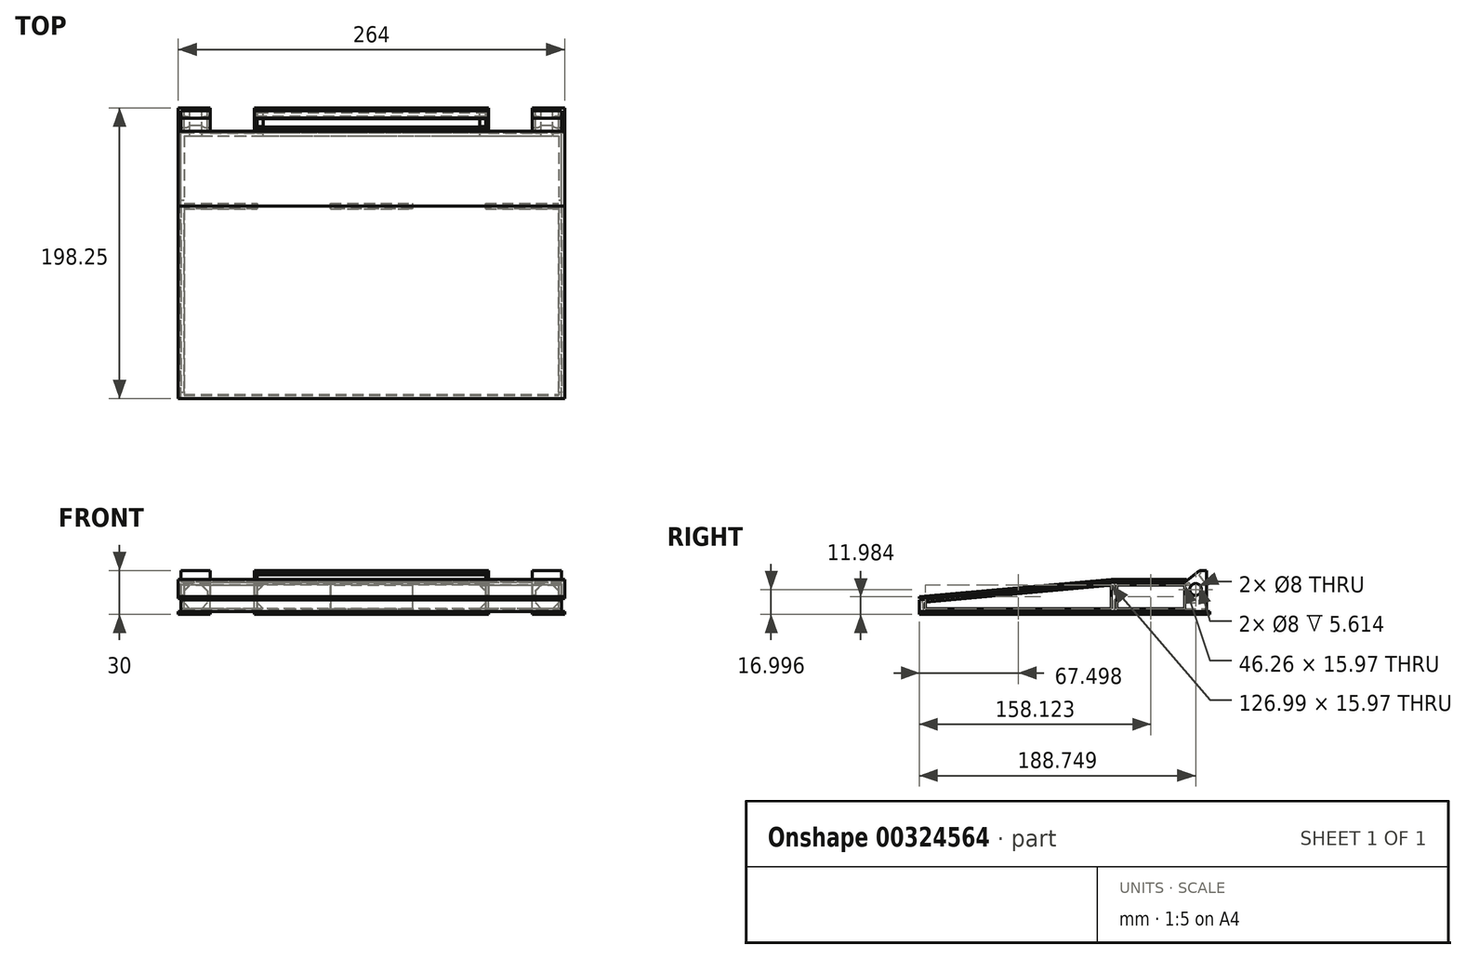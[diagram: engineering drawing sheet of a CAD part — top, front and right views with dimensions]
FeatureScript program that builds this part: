
annotation { "Feature Type Name" : "Feature", "Feature Type Description" : "" }
export const myFeature = defineFeature(function(context is Context, id is Id, definition is map)
    precondition{}
    {
        {
            var Q0;
            Q0=qCreatedBy(makeId("Right.planeOp"),FACE);
            var sketch = newSketch(context, id + "F0", { "sketchPlane" : qUnion([Q0])});
            skLineSegment(sketch, "E0", {"start": v(-99.2, 0) * mm, "end": v(-99.2, 8) * mm});
            skLineSegment(sketch, "E1", {"start": v(-99.2, 8) * mm, "end": v(32.05, 20) * mm});
            skLineSegment(sketch, "E2", {"start": v(32.05, 20) * mm, "end": v(97.05, 20) * mm});
            skLineSegment(sketch, "E3", {"start": v(97.05, 0) * mm, "end": v(97.05, 20) * mm});
            skLineSegment(sketch, "E4", {"start": v(-99.2, 0) * mm, "end": v(97.05, 0) * mm});
            skLineSegment(sketch, "E5", {"start": v(97.05, 20) * mm, "end": v(97.05, 28) * mm});
            skLineSegment(sketch, "E6", {"start": v(97.05, 28) * mm, "end": v(92.05, 28) * mm});
            skLineSegment(sketch, "E7", {"start": v(92.05, 28) * mm, "end": v(82.05, 20) * mm});
            skLineSegment(sketch, "E8", {"start": v(-95.2, 6.36) * mm, "end": v(-95.2, 2) * mm});
            skLineSegment(sketch, "E9", {"start": v(-95.2, 2) * mm, "end": v(31.8, 2) * mm});
            skLineSegment(sketch, "E10", {"start": v(31.8, 2) * mm, "end": v(31.8, 17.97) * mm});
            skLineSegment(sketch, "E11", {"start": v(31.8, 17.97) * mm, "end": v(-95.2, 6.36) * mm});
            skLineSegment(sketch, "E12.bottom", {"start": v(35.8, 17.97) * mm, "end": v(82.05, 17.97) * mm});
            skLineSegment(sketch, "E12.top", {"start": v(35.8, 2) * mm, "end": v(82.05, 2) * mm});
            skLineSegment(sketch, "E12.left", {"start": v(35.8, 17.97) * mm, "end": v(35.8, 2) * mm});
            skLineSegment(sketch, "E12.right", {"start": v(82.05, 17.97) * mm, "end": v(82.05, 2) * mm});
            skLineSegment(sketch, "E13", {"start": v(97.05, 10) * mm, "end": v(82.05, 9.98) * mm});
            skLineSegment(sketch, "E14", {"start": v(-99.2, 9) * mm, "end": v(32.05, 21) * mm});
            skLineSegment(sketch, "E15", {"start": v(32.05, 21) * mm, "end": v(82.05, 21) * mm});
            skLineSegment(sketch, "E16", {"start": v(82.05, 21) * mm, "end": v(83.3, 22) * mm});
            skLineSegment(sketch, "E17", {"start": v(83.3, 22) * mm, "end": v(32, 22) * mm});
            skLineSegment(sketch, "E18", {"start": v(32, 22) * mm, "end": v(-99.2, 10) * mm});
            skLineSegment(sketch, "E19", {"start": v(-99.2, 10) * mm, "end": v(-99.2, 9) * mm});
            skLineSegment(sketch, "E20", {"start": v(32, 23) * mm, "end": v(-98.9, 11.03) * mm});
            skLineSegment(sketch, "E21", {"start": v(-98.9, 11.03) * mm, "end": v(-98.9, 22) * mm});
            skLineSegment(sketch, "E22", {"start": v(88.6, 28) * mm, "end": v(82.35, 23) * mm});
            skLineSegment(sketch, "E23", {"start": v(82.35, 23) * mm, "end": v(32, 23) * mm});
            skLineSegment(sketch, "E24", {"start": v(88.6, 28) * mm, "end": v(-98.9, 28) * mm});
            skLineSegment(sketch, "E25", {"start": v(-98.9, 28) * mm, "end": v(-98.9, 22) * mm});
            skCircle(sketch, "E26", {"center": v(89.55, 15) * mm, "radius": 4 * mm});
            skSolve(sketch);
        }
        {
            var Q0;
            {var subQ0=sQuery(id+"F0.wireOp",EDGE,"E5");Q0=makeQuery(id+"F0.imprint","IMPRINT",FACE,{"disambiguationData":[TD([[makeQuery(id+"F0.imprint","IMPRINT",EDGE,{"derivedFrom":subQ0}),1.0]])]});}
            var Q1;
            Q1=makeQuery(id+"F0.imprint","IMPRINT",FACE,{"disambiguationData":[TD([[makeQuery(id+"F0.imprint","IMPRINT",EDGE,{"derivedFrom":sQuery(id+"F0.wireOp",EDGE,"E0")}),-1.0]])]});
            extrude(context, id + "F1", {"entities" : qUnion([Q0, Q1]), "depth" : 130 * mm, "hasSecondDirection" : true, "secondDirectionOppositeDirection" : true, "secondDirectionDepth" : 130 * mm});
        }
        {
            var Q0;
            Q0=makeQuery(id+"F1.opExtrude","SWEPT_FACE",FACE,{"disambiguationData":[OSD([sQuery(id+"F0.wireOp",EDGE,"E1")])]});
            var sketch = newSketch(context, id + "F2", { "sketchPlane" : qUnion([Q0])});
            skLineSegment(sketch, "E27.top", {"start": v(-130, -98.06) * mm, "end": v(130, -98.06) * mm});
            skLineSegment(sketch, "E28", {"start": v(-130, -98.06) * mm, "end": v(-130, 33.74) * mm});
            skLineSegment(sketch, "E29", {"start": v(-130, 33.74) * mm, "end": v(130, 33.74) * mm});
            skLineSegment(sketch, "E30", {"start": v(130, 33.74) * mm, "end": v(130, -98.06) * mm});
            skLineSegment(sketch, "E31.bottom", {"start": v(-128, 31.74) * mm, "end": v(128, 31.74) * mm});
            skLineSegment(sketch, "E31.top", {"start": v(-128, -96.06) * mm, "end": v(128, -96.06) * mm});
            skLineSegment(sketch, "E31.left", {"start": v(-128, 31.74) * mm, "end": v(-128, -96.06) * mm});
            skLineSegment(sketch, "E31.right", {"start": v(128, 31.74) * mm, "end": v(128, -96.06) * mm});
            skLineSegment(sketch, "E32", {"start": v(-128, 31.74) * mm, "end": v(-128, 33.74) * mm});
            skLineSegment(sketch, "E33", {"start": v(128, 31.74) * mm, "end": v(128, 33.74) * mm});
            skLineSegment(sketch, "E34", {"start": v(-28, 33.74) * mm, "end": v(-28, 31.74) * mm});
            skLineSegment(sketch, "E35", {"start": v(28, 33.74) * mm, "end": v(28, 31.74) * mm});
            skLineSegment(sketch, "E36", {"start": v(78, 33.74) * mm, "end": v(78, 31.74) * mm});
            skLineSegment(sketch, "E37", {"start": v(-78, 33.74) * mm, "end": v(-78, 31.74) * mm});
            skSolve(sketch);
        }
        {
            var Q0;
            Q0=makeQuery(id+"F1.opExtrude","SWEPT_FACE",FACE,{"disambiguationData":[OSD([sQuery(id+"F0.wireOp",EDGE,"E2")])]});
            var sketch = newSketch(context, id + "F3", { "sketchPlane" : qUnion([Q0])});
            skLineSegment(sketch, "E38.bottom", {"start": v(-130, 32.05) * mm, "end": v(130, 32.05) * mm});
            skLineSegment(sketch, "E38.top", {"start": v(-130, 82.05) * mm, "end": v(130, 82.05) * mm});
            skLineSegment(sketch, "E38.left", {"start": v(-130, 32.05) * mm, "end": v(-130, 82.05) * mm});
            skLineSegment(sketch, "E38.right", {"start": v(130, 32.05) * mm, "end": v(130, 82.05) * mm});
            skLineSegment(sketch, "E39.bottom", {"start": v(-128, 80.05) * mm, "end": v(128, 80.05) * mm});
            skLineSegment(sketch, "E39.top", {"start": v(-128, 34.05) * mm, "end": v(128, 34.05) * mm});
            skLineSegment(sketch, "E39.left", {"start": v(-128, 80.05) * mm, "end": v(-128, 34.05) * mm});
            skLineSegment(sketch, "E39.right", {"start": v(128, 80.05) * mm, "end": v(128, 34.05) * mm});
            skLineSegment(sketch, "E40", {"start": v(-78, 32.05) * mm, "end": v(-78, 34.05) * mm});
            skLineSegment(sketch, "E41", {"start": v(-28, 32.05) * mm, "end": v(-28, 34.05) * mm});
            skLineSegment(sketch, "E42", {"start": v(28, 32.05) * mm, "end": v(28, 34.05) * mm});
            skLineSegment(sketch, "E43", {"start": v(78, 32.05) * mm, "end": v(78, 34.05) * mm});
            skSolve(sketch);
        }
        {
            var Q0;
            Q0=makeQuery(id+"F1.opExtrude","SWEPT_FACE",FACE,{"disambiguationData":[OSD([sQuery(id+"F0.wireOp",EDGE,"E7")])]});
            var sketch = newSketch(context, id + "F4", { "sketchPlane" : qUnion([Q0])});
            skLineSegment(sketch, "E44.bottom", {"start": v(-130, 89.37) * mm, "end": v(130, 89.37) * mm});
            skLineSegment(sketch, "E44.top", {"start": v(-130, 76.57) * mm, "end": v(130, 76.57) * mm});
            skLineSegment(sketch, "E44.left", {"start": v(-130, 89.37) * mm, "end": v(-130, 76.57) * mm});
            skLineSegment(sketch, "E44.right", {"start": v(130, 89.37) * mm, "end": v(130, 76.57) * mm});
            skLineSegment(sketch, "E45.bottom", {"start": v(-128, 87.37) * mm, "end": v(128, 87.37) * mm});
            skLineSegment(sketch, "E45.top", {"start": v(-128, 78.57) * mm, "end": v(128, 78.57) * mm});
            skLineSegment(sketch, "E45.left", {"start": v(-128, 87.37) * mm, "end": v(-128, 78.57) * mm});
            skLineSegment(sketch, "E45.right", {"start": v(128, 87.37) * mm, "end": v(128, 78.57) * mm});
            skLineSegment(sketch, "E46", {"start": v(-110, 89.37) * mm, "end": v(-110, 87.37) * mm});
            skLineSegment(sketch, "E47", {"start": v(-80, 89.37) * mm, "end": v(-80, 87.37) * mm});
            skLineSegment(sketch, "E48", {"start": v(110, 89.37) * mm, "end": v(110, 87.37) * mm});
            skLineSegment(sketch, "E49", {"start": v(80, 89.37) * mm, "end": v(80, 87.37) * mm});
            skLineSegment(sketch, "E50", {"start": v(-110, 87.37) * mm, "end": v(-110, 78.57) * mm});
            skLineSegment(sketch, "E51", {"start": v(-110, 78.57) * mm, "end": v(-110, 76.57) * mm});
            skLineSegment(sketch, "E52", {"start": v(-80, 87.37) * mm, "end": v(-80, 78.57) * mm});
            skLineSegment(sketch, "E53", {"start": v(-80, 78.57) * mm, "end": v(-80, 76.57) * mm});
            skLineSegment(sketch, "E54", {"start": v(80, 87.37) * mm, "end": v(80, 78.57) * mm});
            skLineSegment(sketch, "E55", {"start": v(80, 78.57) * mm, "end": v(80, 76.57) * mm});
            skLineSegment(sketch, "E56", {"start": v(110, 87.37) * mm, "end": v(110, 78.57) * mm});
            skLineSegment(sketch, "E57", {"start": v(110, 78.57) * mm, "end": v(110, 76.57) * mm});
            skLineSegment(sketch, "E58", {"start": v(-78, 89.37) * mm, "end": v(-78, 76.57) * mm});
            skLineSegment(sketch, "E59", {"start": v(78, 89.37) * mm, "end": v(78, 76.57) * mm});
            skSolve(sketch);
        }
        {
            var Q0;
            Q0=makeQuery(id+"F1.opExtrude","SWEPT_FACE",FACE,{"disambiguationData":[OSD([sQuery(id+"F0.wireOp",EDGE,"E6")])]});
            var sketch = newSketch(context, id + "F5", { "sketchPlane" : qUnion([Q0])});
            skLineSegment(sketch, "E60.bottom", {"start": v(130, 92.05) * mm, "end": v(-130, 92.05) * mm});
            skLineSegment(sketch, "E60.top", {"start": v(130, 97.05) * mm, "end": v(-130, 97.05) * mm});
            skLineSegment(sketch, "E60.left", {"start": v(130, 92.05) * mm, "end": v(130, 97.05) * mm});
            skLineSegment(sketch, "E60.right", {"start": v(-130, 92.05) * mm, "end": v(-130, 97.05) * mm});
            skLineSegment(sketch, "E61", {"start": v(-110, 97.05) * mm, "end": v(-110, 92.05) * mm});
            skLineSegment(sketch, "E62", {"start": v(-80, 97.05) * mm, "end": v(-80, 92.05) * mm});
            skLineSegment(sketch, "E63.right", {"start": v(80, 97.05) * mm, "end": v(80, 92.05) * mm});
            skLineSegment(sketch, "E64", {"start": v(110, 97.05) * mm, "end": v(110, 92.05) * mm});
            skLineSegment(sketch, "E65", {"start": v(-110, 92.05) * mm, "end": v(-110, 82.05) * mm});
            skLineSegment(sketch, "E66", {"start": v(-110, 82.05) * mm, "end": v(-79.98, 82.05) * mm});
            skLineSegment(sketch, "E67", {"start": v(-79.98, 82.05) * mm, "end": v(-80, 92.05) * mm});
            skLineSegment(sketch, "E68", {"start": v(80, 92.05) * mm, "end": v(80, 82.05) * mm});
            skLineSegment(sketch, "E69", {"start": v(80, 82.05) * mm, "end": v(110, 82.05) * mm});
            skLineSegment(sketch, "E70", {"start": v(110, 82.05) * mm, "end": v(110, 92.05) * mm});
            skLineSegment(sketch, "E71", {"start": v(-79.98, 82.05) * mm, "end": v(80, 82.05) * mm});
            skSolve(sketch);
        }
        {
            var Q0;
            Q0=makeQuery(id+"F3.imprint","IMPRINT",FACE,{"disambiguationData":[TD([[makeQuery(id+"F3.imprint","IMPRINT",EDGE,{"derivedFrom":sQuery(id+"F3.wireOp",EDGE,"E39.bottom")}),-1.0]])]});
            extrude(context, id + "F6", {"entities" : qUnion([Q0]), "operationType" : NewBodyOperationType.REMOVE, "endBound" : BoundingType.THROUGH_ALL, "oppositeDirection" : true, "depth" : 18 * mm});
        }
        {
            var Q0;
            Q0=makeQuery(id+"F2.imprint","IMPRINT",FACE,{"disambiguationData":[TD([[makeQuery(id+"F2.imprint","IMPRINT",EDGE,{"derivedFrom":sQuery(id+"F2.wireOp",EDGE,"E31.bottom")}),-1.0]])]});
            var Q1;
            {var subQ0=sQuery(id+"F2.wireOp",EDGE,"E34");Q1=makeQuery(id+"F2.imprint","IMPRINT",FACE,{"disambiguationData":[TD([[makeQuery(id+"F2.imprint","IMPRINT",EDGE,{"derivedFrom":subQ0}),-1.0]])]});}
            var Q2;
            {var subQ0=sQuery(id+"F3.wireOp",EDGE,"E40");Q2=makeQuery(id+"F3.imprint","IMPRINT",FACE,{"disambiguationData":[TD([[makeQuery(id+"F3.imprint","IMPRINT",EDGE,{"derivedFrom":subQ0}),-1.0]])]});}
            var Q3;
            {var subQ0=sQuery(id+"F2.wireOp",EDGE,"E35");Q3=makeQuery(id+"F2.imprint","IMPRINT",FACE,{"disambiguationData":[TD([[makeQuery(id+"F2.imprint","IMPRINT",EDGE,{"derivedFrom":subQ0}),1.0]])]});}
            var Q4;
            {var subQ0=sQuery(id+"F3.wireOp",EDGE,"E42");Q4=makeQuery(id+"F3.imprint","IMPRINT",FACE,{"disambiguationData":[TD([[makeQuery(id+"F3.imprint","IMPRINT",EDGE,{"derivedFrom":subQ0}),-1.0]])]});}
            extrude(context, id + "F7", {"entities" : qUnion([Q0, Q1, Q2, Q3, Q4]), "operationType" : NewBodyOperationType.REMOVE, "endBound" : BoundingType.THROUGH_ALL, "oppositeDirection" : true, "depth" : 25 * mm, "hasSecondDirection" : true, "secondDirectionOppositeDirection" : false, "secondDirectionDepth" : 8.6 * mm});
        }
        {
            var Q0;
            Q0=makeQuery(id+"F1.opExtrude","SWEPT_FACE",FACE,{"disambiguationData":[OSD([sQuery(id+"F0.wireOp",EDGE,"E4")])]});
            var sketch = newSketch(context, id + "F8", { "sketchPlane" : qUnion([Q0])});
            skLineSegment(sketch, "E72.bottom", {"start": v(-130, 99.2) * mm, "end": v(130, 99.2) * mm});
            skLineSegment(sketch, "E72.top", {"start": v(-130, -97.05) * mm, "end": v(130, -97.05) * mm});
            skLineSegment(sketch, "E72.left", {"start": v(-130, 99.2) * mm, "end": v(-130, -97.05) * mm});
            skLineSegment(sketch, "E72.right", {"start": v(130, 99.2) * mm, "end": v(130, -97.05) * mm});
            skLineSegment(sketch, "E73.bottom", {"start": v(-130, 99.2) * mm, "end": v(-132, 99.2) * mm});
            skLineSegment(sketch, "E73.top", {"start": v(-130, -97.05) * mm, "end": v(-132, -97.05) * mm});
            skLineSegment(sketch, "E73.right", {"start": v(-132, 99.2) * mm, "end": v(-132, -97.05) * mm});
            skLineSegment(sketch, "E74.bottom", {"start": v(130, 99.2) * mm, "end": v(132, 99.2) * mm});
            skLineSegment(sketch, "E74.top", {"start": v(130, -97.05) * mm, "end": v(132, -97.05) * mm});
            skLineSegment(sketch, "E74.right", {"start": v(132, 99.2) * mm, "end": v(132, -97.05) * mm});
            skLineSegment(sketch, "E75.bottom", {"start": v(-132, -97.05) * mm, "end": v(132, -97.05) * mm});
            skLineSegment(sketch, "E75.top", {"start": v(-132, -99.05) * mm, "end": v(132, -99.05) * mm});
            skLineSegment(sketch, "E75.left", {"start": v(-132, -97.05) * mm, "end": v(-132, -99.05) * mm});
            skLineSegment(sketch, "E75.right", {"start": v(132, -97.05) * mm, "end": v(132, -99.05) * mm});
            skLineSegment(sketch, "E76", {"start": v(-110, -97.05) * mm, "end": v(-110, -99.05) * mm});
            skLineSegment(sketch, "E77", {"start": v(-80, -97.05) * mm, "end": v(-80, -99.05) * mm});
            skLineSegment(sketch, "E78", {"start": v(80.02, -97.05) * mm, "end": v(80.02, -99.05) * mm});
            skLineSegment(sketch, "E79", {"start": v(110.02, -97.05) * mm, "end": v(110.02, -99.05) * mm});
            skSolve(sketch);
        }
        {
            var Q0;
            {var subQ1=makeQuery(id+"F1.opExtrude","SWEPT_FACE",FACE,{"disambiguationData":[OSD([sQuery(id+"F0.wireOp",EDGE,"E4")])]});var subQ2=subQ1;var subQ3=makeQuery(id+"F7.opExtrude","SWEPT_FACE",FACE,{"disambiguationData":[OSD([sQuery(id+"F3.wireOp",EDGE,"E42")])]});Q0=makeQuery(id+"F8.imprint","IMPRINT",FACE,{"disambiguationData":[TD([[makeQuery(id+"F8.imprint","IMPRINT",EDGE,{"derivedFrom":makeQuery(id+"F7.boolean.opBoolean","INTERSECT",EDGE,{"derivedFrom":[subQ2,subQ3]})}),1.0]])]});}
            var Q1;
            Q1=makeQuery(id+"F8.imprint","IMPRINT",FACE,{"disambiguationData":[TD([[makeQuery(id+"F8.imprint","IMPRINT",EDGE,{"derivedFrom":sQuery(id+"F8.wireOp",EDGE,"E73.bottom")}),1.0]])]});
            var Q2;
            Q2=makeQuery(id+"F8.imprint","IMPRINT",FACE,{"disambiguationData":[TD([[makeQuery(id+"F8.imprint","IMPRINT",EDGE,{"derivedFrom":sQuery(id+"F8.wireOp",EDGE,"E74.bottom")}),-1.0]])]});
            var Q3;
            {var subQ1=makeQuery(id+"F1.opExtrude","SWEPT_FACE",FACE,{"disambiguationData":[OSD([sQuery(id+"F0.wireOp",EDGE,"E4")])]});var subQ12=makeQuery(id+"F6.opExtrude","SWEPT_FACE",FACE,{"disambiguationData":[OSD([sQuery(id+"F3.wireOp",EDGE,"E39.left")])]});Q3=makeQuery(id+"F8.imprint","IMPRINT",FACE,{"disambiguationData":[TD([[makeQuery(id+"F8.imprint","IMPRINT",EDGE,{"derivedFrom":makeQuery(id+"F6.boolean.opBoolean","INTERSECT",EDGE,{"derivedFrom":[subQ1,subQ12]})}),-1.0]])]});}
            var Q4;
            {var subQ0=sQuery(id+"F8.wireOp",EDGE,"E75.left");Q4=makeQuery(id+"F8.imprint","IMPRINT",FACE,{"disambiguationData":[TD([[makeQuery(id+"F8.imprint","IMPRINT",EDGE,{"derivedFrom":subQ0}),1.0]])]});}
            var Q5;
            {var subQ0=sQuery(id+"F8.wireOp",EDGE,"E75.right");Q5=makeQuery(id+"F8.imprint","IMPRINT",FACE,{"disambiguationData":[TD([[makeQuery(id+"F8.imprint","IMPRINT",EDGE,{"derivedFrom":subQ0}),-1.0]])]});}
            var Q6;
            {var subQ0=sQuery(id+"F8.wireOp",EDGE,"E77");Q6=makeQuery(id+"F8.imprint","IMPRINT",FACE,{"disambiguationData":[TD([[makeQuery(id+"F8.imprint","IMPRINT",EDGE,{"derivedFrom":subQ0}),1.0]])]});}
            var Q7;
            Q7=makeQuery(id+"F8.imprint","IMPRINT",FACE,{"disambiguationData":[TD([[makeQuery(id+"F8.imprint","IMPRINT",EDGE,{"derivedFrom":sQuery(id+"F8.wireOp",EDGE,"E72.bottom")}),1.0]])]});
            extrude(context, id + "F9", {"entities" : qUnion([Q0, Q1, Q2, Q3, Q4, Q5, Q6, Q7]), "operationType" : NewBodyOperationType.ADD, "depth" : 2 * mm});
        }
        {
            var Q0;
            {var subQ0=sQuery(id+"F5.wireOp",EDGE,"E61");Q0=makeQuery(id+"F5.imprint","IMPRINT",FACE,{"disambiguationData":[TD([[makeQuery(id+"F5.imprint","IMPRINT",EDGE,{"derivedFrom":subQ0}),1.0]])]});}
            var Q1;
            {var subQ0=sQuery(id+"F5.wireOp",EDGE,"E65");Q1=makeQuery(id+"F5.imprint","IMPRINT",FACE,{"disambiguationData":[TD([[makeQuery(id+"F5.imprint","IMPRINT",EDGE,{"derivedFrom":subQ0}),1.0]])]});}
            var Q2;
            {var subQ0=sQuery(id+"F5.wireOp",EDGE,"E63.right");Q2=makeQuery(id+"F5.imprint","IMPRINT",FACE,{"disambiguationData":[TD([[makeQuery(id+"F5.imprint","IMPRINT",EDGE,{"derivedFrom":subQ0}),1.0]])]});}
            var Q3;
            {var subQ0=sQuery(id+"F5.wireOp",EDGE,"E68");Q3=makeQuery(id+"F5.imprint","IMPRINT",FACE,{"disambiguationData":[TD([[makeQuery(id+"F5.imprint","IMPRINT",EDGE,{"derivedFrom":subQ0}),1.0]])]});}
            extrude(context, id + "F10", {"entities" : qUnion([Q0, Q1, Q2, Q3]), "operationType" : NewBodyOperationType.REMOVE, "oppositeDirection" : true, "depth" : 30 * mm});
        }
        {
            var Q0;
            {var subQ0=sQuery(id+"F4.wireOp",EDGE,"E58");var subQ1=sQuery(id+"F4.wireOp",EDGE,"E45.bottom");var subQ2=makeQuery(id+"F4.imprint","INTERSECT",VERTEX,{"derivedFrom":[subQ1,subQ0]});Q0=makeQuery(id+"F4.imprint","IMPRINT",FACE,{"disambiguationData":[TD([[makeQuery(id+"F4.imprint","IMPRINT",EDGE,{"disambiguationData":[TD([[subQ2,-1.0]])],"derivedFrom":subQ1}),-1.0]])]});}
            var Q1;
            {var subQ0=sQuery(id+"F4.wireOp",EDGE,"E58");var subQ1=sQuery(id+"F4.wireOp",EDGE,"E44.bottom");var subQ2=makeQuery(id+"F4.imprint","INTERSECT",VERTEX,{"derivedFrom":[subQ1,subQ0]});Q1=makeQuery(id+"F4.imprint","IMPRINT",FACE,{"disambiguationData":[TD([[makeQuery(id+"F4.imprint","IMPRINT",EDGE,{"disambiguationData":[TD([[subQ2,1.0]])],"derivedFrom":subQ1}),1.0]])]});}
            var Q2;
            {var subQ0=sQuery(id+"F4.wireOp",EDGE,"E58");var subQ1=sQuery(id+"F4.wireOp",EDGE,"E44.top");var subQ2=makeQuery(id+"F4.imprint","INTERSECT",VERTEX,{"derivedFrom":[subQ1,subQ0]});Q2=makeQuery(id+"F4.imprint","IMPRINT",FACE,{"disambiguationData":[TD([[makeQuery(id+"F4.imprint","IMPRINT",EDGE,{"disambiguationData":[TD([[subQ2,1.0]])],"derivedFrom":subQ1}),-1.0]])]});}
            extrude(context, id + "F11", {"entities" : qUnion([Q0, Q1, Q2]), "operationType" : NewBodyOperationType.REMOVE, "depth" : -2 * mm});
        }
        {
            var Q0;
            {var subQ0=sQuery(id+"F4.wireOp",EDGE,"E58");var subQ1=sQuery(id+"F4.wireOp",EDGE,"E45.bottom");var subQ2=makeQuery(id+"F4.imprint","INTERSECT",VERTEX,{"derivedFrom":[subQ1,subQ0]});Q0=makeQuery(id+"F4.imprint","IMPRINT",FACE,{"disambiguationData":[TD([[makeQuery(id+"F4.imprint","IMPRINT",EDGE,{"disambiguationData":[TD([[subQ2,-1.0]])],"derivedFrom":subQ1}),-1.0]])]});}
            extrude(context, id + "F12", {"entities" : qUnion([Q0]), "operationType" : NewBodyOperationType.REMOVE, "depth" : -8.5 * mm});
        }
        {
            var Q0;
            Q0=makeQuery(id+"F10.boolean.opBoolean","SPLIT",FACE,{"disambiguationData":[TD([makeQuery(id+"F10.opExtrude","SWEPT_FACE",FACE,{"disambiguationData":[OSD([sQuery(id+"F5.wireOp",EDGE,"E62")])]})])],"derivedFrom":makeQuery(id+"F1.opExtrude","SWEPT_FACE",FACE,{"disambiguationData":[OSD([sQuery(id+"F0.wireOp",EDGE,"E3"),sQuery(id+"F0.wireOp",EDGE,"E5")])]})});
            var sketch = newSketch(context, id + "F13", { "sketchPlane" : qUnion([Q0])});
            skLineSegment(sketch, "E80.bottom", {"start": v(-78, 2) * mm, "end": v(78, 2) * mm});
            skLineSegment(sketch, "E80.top", {"start": v(-78, 18) * mm, "end": v(78, 18) * mm});
            skLineSegment(sketch, "E80.left", {"start": v(-78, 2) * mm, "end": v(-78, 18) * mm});
            skLineSegment(sketch, "E80.right", {"start": v(78, 2) * mm, "end": v(78, 18) * mm});
            skLineSegment(sketch, "E81", {"start": v(-78, 14) * mm, "end": v(-74, 18) * mm});
            skLineSegment(sketch, "E82", {"start": v(-78, 6) * mm, "end": v(-74, 2) * mm});
            skLineSegment(sketch, "E83", {"start": v(74, 18) * mm, "end": v(78, 14) * mm});
            skLineSegment(sketch, "E84", {"start": v(78, 6) * mm, "end": v(74, 2) * mm});
            skLineSegment(sketch, "E85.bottom", {"start": v(112, 18) * mm, "end": v(128, 18) * mm});
            skLineSegment(sketch, "E85.top", {"start": v(112, 2) * mm, "end": v(128, 2) * mm});
            skLineSegment(sketch, "E85.left", {"start": v(112, 18) * mm, "end": v(112, 2) * mm});
            skLineSegment(sketch, "E85.right", {"start": v(128, 18) * mm, "end": v(128, 2) * mm});
            skLineSegment(sketch, "E86", {"start": v(112, 14) * mm, "end": v(116, 18) * mm});
            skLineSegment(sketch, "E87", {"start": v(124, 18) * mm, "end": v(128, 14) * mm});
            skLineSegment(sketch, "E88", {"start": v(112, 6) * mm, "end": v(116, 2) * mm});
            skLineSegment(sketch, "E89", {"start": v(124, 2) * mm, "end": v(128, 6) * mm});
            skLineSegment(sketch, "E90.bottom", {"start": v(-128, 18) * mm, "end": v(-112, 18) * mm});
            skLineSegment(sketch, "E90.top", {"start": v(-128, 2) * mm, "end": v(-112, 2) * mm});
            skLineSegment(sketch, "E90.left", {"start": v(-128, 18) * mm, "end": v(-128, 2) * mm});
            skLineSegment(sketch, "E90.right", {"start": v(-112, 18) * mm, "end": v(-112, 2) * mm});
            skLineSegment(sketch, "E91", {"start": v(-124, 18) * mm, "end": v(-128, 14) * mm});
            skLineSegment(sketch, "E92", {"start": v(-128, 6) * mm, "end": v(-124, 2) * mm});
            skLineSegment(sketch, "E93", {"start": v(-116, 18) * mm, "end": v(-112, 14) * mm});
            skLineSegment(sketch, "E94", {"start": v(-112, 6) * mm, "end": v(-116, 2) * mm});
            skLineSegment(sketch, "E95.bottom", {"start": v(-128, 18) * mm, "end": v(130, 18) * mm});
            skLineSegment(sketch, "E95.top", {"start": v(-130, 28) * mm, "end": v(130, 28) * mm});
            skLineSegment(sketch, "E95.right", {"start": v(130, 18) * mm, "end": v(130, 28) * mm});
            skLineSegment(sketch, "E96", {"start": v(-130, 28) * mm, "end": v(-130, 0) * mm});
            skLineSegment(sketch, "E97", {"start": v(-130, 0) * mm, "end": v(130, 0) * mm});
            skLineSegment(sketch, "E98", {"start": v(130, 0) * mm, "end": v(130, 18) * mm});
            skSolve(sketch);
        }
        {
            var Q0;
            {var subQ3=sQuery(id+"F13.wireOp",EDGE,"E91");Q0=makeQuery(id+"F13.imprint","IMPRINT",FACE,{"disambiguationData":[TD([[makeQuery(id+"F13.imprint","IMPRINT",EDGE,{"derivedFrom":subQ3}),1.0]])]});}
            var Q1;
            {var subQ3=sQuery(id+"F13.wireOp",EDGE,"E81");Q1=makeQuery(id+"F13.imprint","IMPRINT",FACE,{"disambiguationData":[TD([[makeQuery(id+"F13.imprint","IMPRINT",EDGE,{"derivedFrom":subQ3}),-1.0]])]});}
            var Q2;
            {var subQ3=sQuery(id+"F13.wireOp",EDGE,"E86");Q2=makeQuery(id+"F13.imprint","IMPRINT",FACE,{"disambiguationData":[TD([[makeQuery(id+"F13.imprint","IMPRINT",EDGE,{"derivedFrom":subQ3}),-1.0]])]});}
            extrude(context, id + "F14", {"entities" : qUnion([Q0, Q1, Q2]), "operationType" : NewBodyOperationType.REMOVE, "depth" : -20 * mm});
        }
        {
            var Q0;
            Q0=makeQuery(id+"F0.imprint","IMPRINT",FACE,{"disambiguationData":[TD([[makeQuery(id+"F0.imprint","IMPRINT",EDGE,{"derivedFrom":sQuery(id+"F0.wireOp",EDGE,"E14")}),1.0]])]});
            extrude(context, id + "F15", {"entities" : qUnion([Q0]), "depth" : 132 * mm, "hasSecondDirection" : true, "secondDirectionOppositeDirection" : true, "secondDirectionDepth" : 132 * mm});
        }
    });
